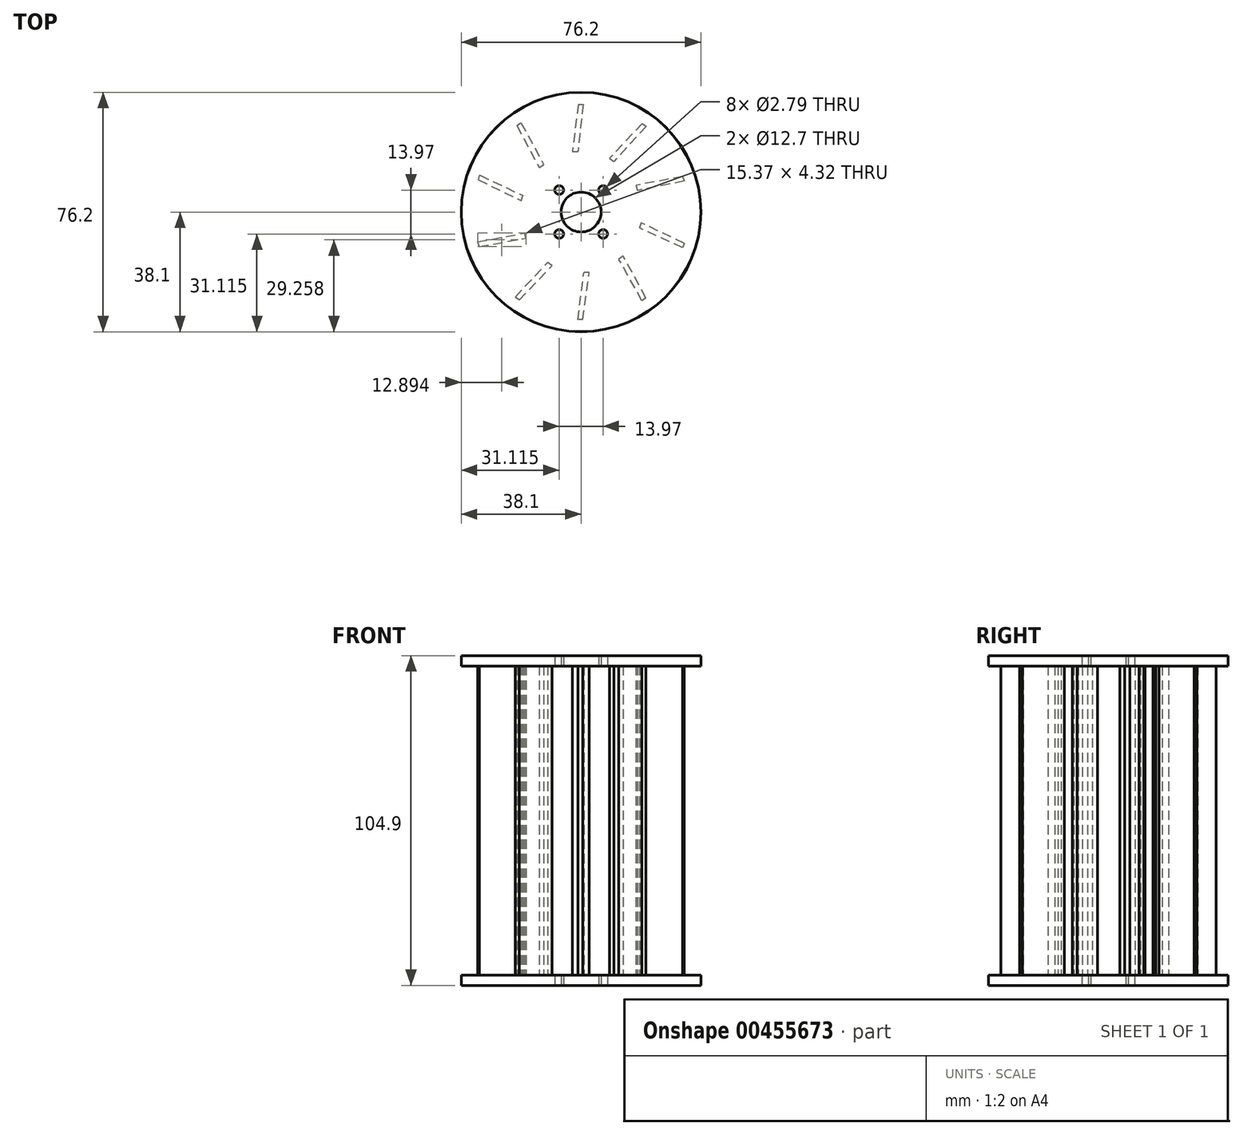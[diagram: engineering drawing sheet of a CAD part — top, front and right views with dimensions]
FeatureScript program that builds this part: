
annotation { "Feature Type Name" : "Feature", "Feature Type Description" : "" }
export const myFeature = defineFeature(function(context is Context, id is Id, definition is map)
    precondition{}
    {
        {
            var Q0;
            Q0=qCreatedBy(makeId("Top.planeOp"),FACE);
            var sketch = newSketch(context, id + "F0", { "sketchPlane" : qUnion([Q0])});
            skCircle(sketch, "E0", {"center": v(0, 0) * mm, "radius": 3.18 * mm});
            skCircle(sketch, "E1", {"center": v(0, 0) * mm, "radius": 38.1 * mm});
            skLineSegment(sketch, "E2", {"start": v(-0.9, 34.23) * mm, "end": v(0.65, 34.23) * mm});
            skLineSegment(sketch, "E3", {"start": v(0.65, 34.23) * mm, "end": v(-1.05, 19.2) * mm});
            skLineSegment(sketch, "E4", {"start": v(-0.9, 34.23) * mm, "end": v(-2.75, 19.2) * mm});
            skLineSegment(sketch, "E5", {"start": v(-2.75, 19.2) * mm, "end": v(-1.05, 19.2) * mm});
            skLineSegment(sketch, "E6.1.0", {"start": v(20.7, 27.27) * mm, "end": v(10.47, 16.13) * mm});
            skLineSegment(sketch, "E6.1.1", {"start": v(19.44, 28.19) * mm, "end": v(9.1, 17.13) * mm});
            skLineSegment(sketch, "E6.1.2", {"start": v(19.44, 28.19) * mm, "end": v(20.7, 27.27) * mm});
            skLineSegment(sketch, "E6.1.3", {"start": v(9.1, 17.13) * mm, "end": v(10.47, 16.13) * mm});
            skLineSegment(sketch, "E6.2.0", {"start": v(32.8, 9.83) * mm, "end": v(17.96, 6.86) * mm});
            skLineSegment(sketch, "E6.2.1", {"start": v(32.32, 11.31) * mm, "end": v(17.44, 8.48) * mm});
            skLineSegment(sketch, "E6.2.2", {"start": v(32.32, 11.31) * mm, "end": v(32.8, 9.83) * mm});
            skLineSegment(sketch, "E6.2.3", {"start": v(17.44, 8.48) * mm, "end": v(17.96, 6.86) * mm});
            skLineSegment(sketch, "E6.3.0", {"start": v(32.29, -11.39) * mm, "end": v(18.55, -5.04) * mm});
            skLineSegment(sketch, "E6.3.1", {"start": v(32.78, -9.9) * mm, "end": v(19.09, -3.43) * mm});
            skLineSegment(sketch, "E6.3.2", {"start": v(32.78, -9.9) * mm, "end": v(32.29, -11.39) * mm});
            skLineSegment(sketch, "E6.3.3", {"start": v(19.09, -3.43) * mm, "end": v(18.55, -5.04) * mm});
            skLineSegment(sketch, "E6.4.0", {"start": v(19.37, -28.23) * mm, "end": v(12.02, -15) * mm});
            skLineSegment(sketch, "E6.4.1", {"start": v(20.64, -27.32) * mm, "end": v(13.4, -14.02) * mm});
            skLineSegment(sketch, "E6.4.2", {"start": v(20.64, -27.32) * mm, "end": v(19.37, -28.23) * mm});
            skLineSegment(sketch, "E6.4.3", {"start": v(13.4, -14.02) * mm, "end": v(12.02, -15) * mm});
            skLineSegment(sketch, "E6.5.0", {"start": v(-0.99, -34.22) * mm, "end": v(0.86, -19.2) * mm});
            skLineSegment(sketch, "E6.5.1", {"start": v(0.57, -34.24) * mm, "end": v(2.56, -19.22) * mm});
            skLineSegment(sketch, "E6.5.2", {"start": v(0.57, -34.24) * mm, "end": v(-0.99, -34.22) * mm});
            skLineSegment(sketch, "E6.5.3", {"start": v(2.56, -19.22) * mm, "end": v(0.86, -19.2) * mm});
            skLineSegment(sketch, "E6.6.0", {"start": v(-20.97, -27.07) * mm, "end": v(-10.62, -16.02) * mm});
            skLineSegment(sketch, "E6.6.1", {"start": v(-19.71, -28) * mm, "end": v(-9.26, -17.04) * mm});
            skLineSegment(sketch, "E6.6.2", {"start": v(-19.71, -28) * mm, "end": v(-20.97, -27.07) * mm});
            skLineSegment(sketch, "E6.6.3", {"start": v(-9.26, -17.04) * mm, "end": v(-10.62, -16.02) * mm});
            skLineSegment(sketch, "E6.7.0", {"start": v(-32.89, -9.5) * mm, "end": v(-18.03, -6.68) * mm});
            skLineSegment(sketch, "E6.7.1", {"start": v(-32.43, -11) * mm, "end": v(-17.52, -8.3) * mm});
            skLineSegment(sketch, "E6.7.2", {"start": v(-32.43, -11) * mm, "end": v(-32.89, -9.5) * mm});
            skLineSegment(sketch, "E6.7.3", {"start": v(-17.52, -8.3) * mm, "end": v(-18.03, -6.68) * mm});
            skLineSegment(sketch, "E6.8.0", {"start": v(-32.17, 11.7) * mm, "end": v(-18.5, 5.22) * mm});
            skLineSegment(sketch, "E6.8.1", {"start": v(-32.68, 10.22) * mm, "end": v(-19.05, 3.61) * mm});
            skLineSegment(sketch, "E6.8.2", {"start": v(-32.68, 10.22) * mm, "end": v(-32.17, 11.7) * mm});
            skLineSegment(sketch, "E6.8.3", {"start": v(-19.05, 3.61) * mm, "end": v(-18.5, 5.22) * mm});
            skLineSegment(sketch, "E6.9.0", {"start": v(-19.1, 28.41) * mm, "end": v(-11.87, 15.13) * mm});
            skLineSegment(sketch, "E6.9.1", {"start": v(-20.38, 27.52) * mm, "end": v(-13.26, 14.15) * mm});
            skLineSegment(sketch, "E6.9.2", {"start": v(-20.38, 27.52) * mm, "end": v(-19.1, 28.41) * mm});
            skLineSegment(sketch, "E6.9.3", {"start": v(-13.26, 14.15) * mm, "end": v(-11.87, 15.13) * mm});
            skLineSegment(sketch, "E6.anchor1", {"start": v(0, 0) * mm, "end": v(-2.75, 19.2) * mm, "construction": true});
            skLineSegment(sketch, "E6.anchor2", {"start": v(0, 0) * mm, "end": v(-13.26, 14.15) * mm, "construction": true});
            skSolve(sketch);
        }
        {
            var Q0;
            Q0=makeQuery(id+"F0.imprint","IMPRINT",FACE,{"disambiguationData":[TD([[makeQuery(id+"F0.imprint","IMPRINT",EDGE,{"derivedFrom":sQuery(id+"F0.wireOp",EDGE,"E0")}),-1.0]])]});
            extrude(context, id + "F1", {"entities" : qUnion([Q0]), "depth" : 3.3 * mm});
        }
        {
            var Q0;
            Q0=makeQuery(id+"F0.imprint","IMPRINT",FACE,{"disambiguationData":[TD([[makeQuery(id+"F0.imprint","IMPRINT",EDGE,{"derivedFrom":sQuery(id+"F0.wireOp",EDGE,"E6.8.0")}),-1.0]])]});
            var Q1;
            Q1=makeQuery(id+"F0.imprint","IMPRINT",FACE,{"disambiguationData":[TD([[makeQuery(id+"F0.imprint","IMPRINT",EDGE,{"derivedFrom":sQuery(id+"F0.wireOp",EDGE,"E6.7.0")}),-1.0]])]});
            var Q2;
            Q2=makeQuery(id+"F0.imprint","IMPRINT",FACE,{"disambiguationData":[TD([[makeQuery(id+"F0.imprint","IMPRINT",EDGE,{"derivedFrom":sQuery(id+"F0.wireOp",EDGE,"E6.6.0")}),-1.0]])]});
            var Q3;
            Q3=makeQuery(id+"F0.imprint","IMPRINT",FACE,{"disambiguationData":[TD([[makeQuery(id+"F0.imprint","IMPRINT",EDGE,{"derivedFrom":sQuery(id+"F0.wireOp",EDGE,"E6.5.0")}),-1.0]])]});
            var Q4;
            Q4=makeQuery(id+"F0.imprint","IMPRINT",FACE,{"disambiguationData":[TD([[makeQuery(id+"F0.imprint","IMPRINT",EDGE,{"derivedFrom":sQuery(id+"F0.wireOp",EDGE,"E6.4.0")}),-1.0]])]});
            var Q5;
            Q5=makeQuery(id+"F0.imprint","IMPRINT",FACE,{"disambiguationData":[TD([[makeQuery(id+"F0.imprint","IMPRINT",EDGE,{"derivedFrom":sQuery(id+"F0.wireOp",EDGE,"E6.3.0")}),-1.0]])]});
            var Q6;
            Q6=makeQuery(id+"F0.imprint","IMPRINT",FACE,{"disambiguationData":[TD([[makeQuery(id+"F0.imprint","IMPRINT",EDGE,{"derivedFrom":sQuery(id+"F0.wireOp",EDGE,"E6.2.0")}),-1.0]])]});
            var Q7;
            Q7=makeQuery(id+"F0.imprint","IMPRINT",FACE,{"disambiguationData":[TD([[makeQuery(id+"F0.imprint","IMPRINT",EDGE,{"derivedFrom":sQuery(id+"F0.wireOp",EDGE,"E6.1.0")}),-1.0]])]});
            var Q8;
            Q8=makeQuery(id+"F0.imprint","IMPRINT",FACE,{"disambiguationData":[TD([[makeQuery(id+"F0.imprint","IMPRINT",EDGE,{"derivedFrom":sQuery(id+"F0.wireOp",EDGE,"E2")}),-1.0]])]});
            var Q9;
            Q9=makeQuery(id+"F0.imprint","IMPRINT",FACE,{"disambiguationData":[TD([[makeQuery(id+"F0.imprint","IMPRINT",EDGE,{"derivedFrom":sQuery(id+"F0.wireOp",EDGE,"E6.9.0")}),-1.0]])]});
            extrude(context, id + "F2", {"entities" : qUnion([Q0, Q1, Q2, Q3, Q4, Q5, Q6, Q7, Q8, Q9]), "operationType" : NewBodyOperationType.ADD, "depth" : 101.6 * mm, "offsetDistance" : 25.4 * mm});
        }
        {
            var Q0;
            Q0=makeQuery(id+"F2.opExtrude","CAP_FACE",FACE,{"disambiguationData":[OSD([sQuery(id+"F0.wireOp",EDGE,"E6.7.0"),sQuery(id+"F0.wireOp",EDGE,"E6.7.1"),sQuery(id+"F0.wireOp",EDGE,"E6.7.2"),sQuery(id+"F0.wireOp",EDGE,"E6.7.3")])],"isStart":false});
            var sketch = newSketch(context, id + "F3", { "sketchPlane" : qUnion([Q0])});
            skCircle(sketch, "E7", {"center": v(0, 0) * mm, "radius": 38.08 * mm});
            skCircle(sketch, "E8", {"center": v(0, 0) * mm, "radius": 3.18 * mm});
            skSolve(sketch);
        }
        {
            var Q0;
            Q0 = qSketchRegion(id + "F3", true);
            extrude(context, id + "F4", {"entities" : qUnion([Q0]), "operationType" : NewBodyOperationType.ADD, "depth" : 3.3 * mm});
        }
        {
            var Q0;
            Q0=makeQuery(id+"F4.opExtrude","CAP_FACE",FACE,{"disambiguationData":[OSD([sQuery(id+"F3.wireOp",EDGE,"E7"),sQuery(id+"F3.wireOp",EDGE,"E8")])],"isStart":false});
            var sketch = newSketch(context, id + "F5", { "sketchPlane" : qUnion([Q0])});
            skSolve(sketch);
        }
        {
            var Q0;
            Q0=makeQuery(id+"F0.imprint","IMPRINT",FACE,{"disambiguationData":[TD([[makeQuery(id+"F0.imprint","IMPRINT",EDGE,{"derivedFrom":sQuery(id+"F0.wireOp",EDGE,"E0")}),-1.0]])]});
            var sketch = newSketch(context, id + "F6", { "sketchPlane" : qUnion([Q0])});
            skPoint(sketch, "E9.middle", {"position": v(0, 0) * mm});
            skCircle(sketch, "E10", {"center": v(6.99, -6.99) * mm, "radius": 1.4 * mm});
            skCircle(sketch, "E11.MirrorC", {"center": v(-6.99, -6.99) * mm, "radius": 1.4 * mm});
            skCircle(sketch, "E12.MirrorC", {"center": v(-6.99, 6.99) * mm, "radius": 1.4 * mm});
            skCircle(sketch, "E13.MirrorC", {"center": v(6.99, 6.99) * mm, "radius": 1.4 * mm});
            skCircle(sketch, "E14", {"center": v(0, 0) * mm, "radius": 6.35 * mm});
            skSolve(sketch);
        }
        {
            var Q0;
            Q0 = qSketchRegion(id + "F6", true);
            extrude(context, id + "F7", {"entities" : qUnion([Q0]), "operationType" : NewBodyOperationType.REMOVE, "depth" : 136.9 * mm, "offsetDistance" : 25.4 * mm});
        }
    });
